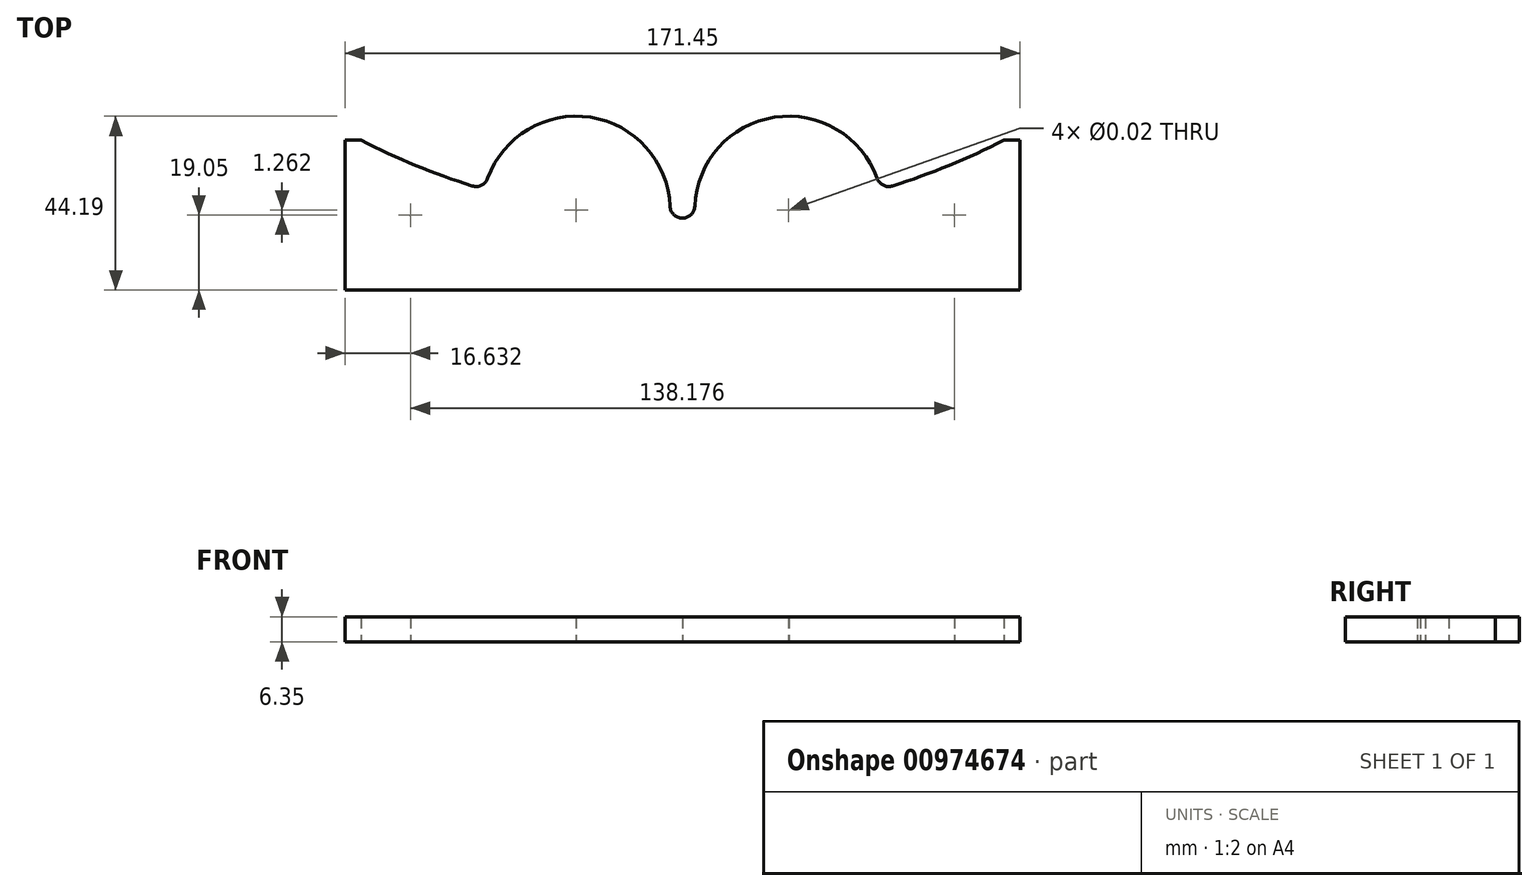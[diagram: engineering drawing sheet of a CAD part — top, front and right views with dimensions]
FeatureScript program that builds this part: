
annotation { "Feature Type Name" : "Feature", "Feature Type Description" : "" }
export const myFeature = defineFeature(function(context is Context, id is Id, definition is map)
    precondition{}
    {
        {
            var Q0;
            Q0=qCreatedBy(makeId("Top.planeOp"),FACE);
            var sketch = newSketch(context, id + "F0", { "sketchPlane" : qUnion([Q0])});
            skLineSegment(sketch, "E0.bottom", {"start": v(-85.73, 19.05) * mm, "end": v(-81.64, 19.05) * mm});
            skLineSegment(sketch, "E0.top", {"start": v(-85.73, -19.05) * mm, "end": v(85.73, -19.05) * mm});
            skLineSegment(sketch, "E0.left", {"start": v(-85.73, 19.05) * mm, "end": v(-85.73, -19.05) * mm});
            skLineSegment(sketch, "E0.right", {"start": v(85.73, 19.05) * mm, "end": v(85.73, -19.05) * mm});
            skPoint(sketch, "E0.middle", {"position": v(0, 0) * mm});
            skLineSegment(sketch, "E1", {"start": v(-134.55, 0) * mm, "end": v(120.86, 0) * mm, "construction": true});
            skPoint(sketch, "E1.startSnap0", {"position": v(-85.73, 0) * mm});
            skLineSegment(sketch, "E2", {"start": v(0, 177) * mm, "end": v(0, -88.85) * mm, "construction": true});
            skLineSegment(sketch, "E3.0", {"start": v(-134.55, 177) * mm, "end": v(120.86, 177) * mm, "construction": true});
            skPoint(sketch, "E4.orphan", {"position": v(0, 100.83) * mm});
            skArc(sketch, "E5", {"start": v(-81.64, 19.05) * mm, "mid": v(-66.27, 12.01) * mm, "end": v(-50.3, 6.46) * mm});
            skLineSegment(sketch, "E6.0", {"start": v(-27, 177) * mm, "end": v(-27, -88.85) * mm, "construction": true});
            skArc(sketch, "E7", {"start": v(-3.21, -0.77) * mm, "mid": v(-26.61, 25.13) * mm, "end": v(-50.84, 0) * mm});
            skArc(sketch, "E8.MirrorC", {"start": v(3.21, -0.77) * mm, "mid": v(23.37, 24.86) * mm, "end": v(50.3, 6.46) * mm});
            skLineSegment(sketch, "E9.trimOffspring", {"start": v(81.64, 19.05) * mm, "end": v(85.73, 19.05) * mm});
            skLineSegment(sketch, "E10.trimOffspring", {"start": v(11.07, 19.05) * mm, "end": v(42.93, 19.05) * mm});
            skArc(sketch, "E11.trimOffspring", {"start": v(50.3, 6.46) * mm, "mid": v(66.27, 12.01) * mm, "end": v(81.64, 19.05) * mm});
            skArc(sketch, "E12.trimOffspring", {"start": v(-3.21, -0.77) * mm, "mid": v(0, -0.8) * mm, "end": v(3.21, -0.77) * mm});
            skArc(sketch, "E13.trimOffspring", {"start": v(-39.55, -19.05) * mm, "mid": v(-33.52, -21.7) * mm, "end": v(-27, -22.61) * mm});
            skLineSegment(sketch, "E14.trimOffspring", {"start": v(-42.93, 19.05) * mm, "end": v(0, 19.05) * mm});
            skLineSegment(sketch, "E15.0", {"start": v(-69.09, 177) * mm, "end": v(-69.09, -88.85) * mm, "construction": true});
            skPoint(sketch, "E16", {"position": v(-69.09, 0) * mm});
            skPoint(sketch, "E17.MirrorP", {"position": v(69.09, 0) * mm});
            skSolve(sketch);
        }
        {
            var Q0;
            Q0 = qSketchRegion(id + "F0", true);
            extrude(context, id + "F1", {"entities" : qUnion([Q0]), "depth" : 6.35 * mm, "offsetDistance" : 25.4 * mm});
        }
        {
            var Q0;
            Q0=makeQuery(id+"F1.opExtrude","SWEPT_EDGE",EDGE,{"disambiguationData":[OSD([sQuery(id+"F0.wireOp",EDGE,"E8.MirrorC"),sQuery(id+"F0.wireOp",EDGE,"E11.trimOffspring")])]});
            var Q1;
            Q1=makeQuery(id+"F1.opExtrude","SWEPT_EDGE",EDGE,{"disambiguationData":[OSD([sQuery(id+"F0.wireOp",EDGE,"E8.MirrorC"),sQuery(id+"F0.wireOp",EDGE,"E12.trimOffspring")])]});
            var Q2;
            Q2=makeQuery(id+"F1.opExtrude","SWEPT_EDGE",EDGE,{"disambiguationData":[OSD([sQuery(id+"F0.wireOp",EDGE,"E7"),sQuery(id+"F0.wireOp",EDGE,"E12.trimOffspring")])]});
            var Q3;
            Q3=makeQuery(id+"F1.opExtrude","SWEPT_EDGE",EDGE,{"disambiguationData":[OSD([sQuery(id+"F0.wireOp",EDGE,"E5"),sQuery(id+"F0.wireOp",EDGE,"E7")])]});
            fillet(context, id + "F2", {"entities" : qUnion([Q0, Q1, Q2, Q3]), "radius" : 3.17 * mm, "tangentPropagation" : true, "allowEdgeOverflow" : false});
        }
        {
            var Q0;
            Q0=sQuery(id+"F0.wireOp",VERTEX,"E16");
            var Q1;
            Q1=sQuery(id+"F0.wireOp",VERTEX,"E7.center");
            var Q2;
            Q2=sQuery(id+"F0.wireOp",VERTEX,"E8.MirrorC.center");
            var Q3;
            Q3=sQuery(id+"F0.wireOp",VERTEX,"E17.MirrorP");
            var Q4;
            Q4=makeQuery(id+"F1.opExtrude","SWEPT_BODY",BODY,{"disambiguationData":[OSD([sQuery(id+"F0.wireOp",EDGE,"E0.bottom"),sQuery(id+"F0.wireOp",EDGE,"E0.top"),sQuery(id+"F0.wireOp",EDGE,"E0.left"),sQuery(id+"F0.wireOp",EDGE,"E0.right"),sQuery(id+"F0.wireOp",EDGE,"E5"),sQuery(id+"F0.wireOp",EDGE,"E7"),sQuery(id+"F0.wireOp",EDGE,"E8.MirrorC"),sQuery(id+"F0.wireOp",EDGE,"E9.trimOffspring"),sQuery(id+"F0.wireOp",EDGE,"E11.trimOffspring"),sQuery(id+"F0.wireOp",EDGE,"E12.trimOffspring")])]});
            hole(context, id + "F3", {"style" : HoleStyle.SIMPLE, "endStyle" : HoleEndStyle.THROUGH, "oppositeDirection" : true, "standardTappedOrClearance" : lookupTablePath({ "standard" : "ANSI", "size" : "9/16 (0.56)", "type" : "Drilled" }), "standardBlindInLast" : lookupTablePath({ "standard" : "ANSI", "size" : "9/16 (0.56)", "type" : "Drilled" }), "holeDiameter" : 9 / 406.4 * mm, "majorDiameter" : 6.35 * mm, "isTappedThrough" : true, "tappedDepth" : 7.9 * mm, "tapClearance" : 3, "startFromSketch" : true, "locations" : qUnion([Q0, Q1, Q2, Q3]), "scope" : qUnion([Q4])});
        }
    });
